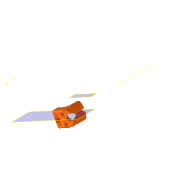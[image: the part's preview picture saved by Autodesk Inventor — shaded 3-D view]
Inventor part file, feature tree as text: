
AUTODESK INVENTOR PART (.ipt)
format: ipt  version: 2022 (Build 260153000, 153)  size: 468,992 bytes
history: native  units: in
note: dims shown in document units (in); Inventor stores cm internally (conversion verified against a paired STEP export)
features: sketch x13, extrude x9, other x8, reference x8, projected_geometry x3, plane x2, fillet x2, hole x2
ambient origin geometry x8: Origin, YZ Plane, XZ Plane, XY Plane, X Axis, Y Axis, Z Axis, Center Point
bodies: Solid1 (feature_tree)
feature tree (47):
  plane  "Work Plane1"
  extrude  "Extrusion1"  Depth=0.5307in
  sketch  "Skizze18"  dims[d23=0.2653in d25=135.0deg d26=0.1575in]
  plane  "Arbeitsebene3"
  other  "Arbeitsachse1"
  extrude  "Extrusion17"  TaperAngle=135.0deg  [1 undecoded]
  fillet  "Rundung4"  Radius=0.1575in
  hole  "Bohrung1"  [1 undecoded]
  extrude  "Extrusion19"  Depth=0.0591in
  hole  "Bohrung2"  [1 undecoded]
  extrude  "Extrusion20"  Depth=0.1181in
  extrude  "Extrusion21"  Depth=0.1102in
  extrude  "Extrusion22"  TaperAngle=0.0deg  [1 undecoded]
  fillet  "Rundung6"  Radius=0.4921in
  sketch  "Skizze27"  dims[d97=0.0in d98=0.0in d100=0.3937in d101=0.0in]
  extrude  "Extrusion23"  Depth=0.1575in
  extrude  "Extrusion24"  Depth=0.3937in TaperAngle=0.0deg
  extrude  "Extrusion25"  Depth=0.1575in
  sketch  "Sketch1"  dims[d0=1.1811in d1=0.0in d22=0.5307in]
  reference  "Reference1"
  sketch  "Skizze19"  dims[d27=0.2362in d29=0.3937in]
  reference  "Referenz6"
  sketch  "Skizze20"  dims[d31=0.5906in d40=0.0591in]
  reference  "Referenz7"
  reference  "Referenz8"
  sketch  "Skizze22"  dims[d42=1.378in d70=0.4724in]
  projected_geometry  "Projizierte Kontur13"
  projected_geometry  "Projizierte Kontur14"
  sketch  "Skizze23"  dims[d71=0.0in d72=-0.0069in d73=0.1181in]
  sketch  "Skizze24"  dims[d74=0.126in d75=0.2362in d76=0.2756in d77=1.1811in d78=90.0deg d79=0.315in d80=0.8108in d84=0.1102in]
  reference  "Referenz9"
  reference  "Referenz10"
  sketch  "Skizze25"  dims[d85=0.1102in d86=0.0in d87=0.0in d88=0.4921in]
  sketch  "Skizze26"  dims[d89=0.4921in d90=0.2362in d91=0.1575in d92=0.0787in d93=90.0deg d94=0.5118in d95=0.8108in d96=0.1575in]
  reference  "Referenz11"
  reference  "Referenz12"
  sketch  "Skizze28"  dims[d102=0.0in d103=0.0in d104=0.1575in]
  projected_geometry  "Projizierte Kontur15"
  sketch  "Skizze29"  dims[d105=0.6299in]
  sketch  "Skizze30"  dims[d106=0.6299in d107=0.1181in d108=0.1102in d109=0.1102in d110=0.0in d111=0.0in d112=45.0deg d113=0.0in d114=0.0in d115=0.1102in d116=0.1102in d117=0.3937in d118=0.0in]
  other  "<userpath>\Documents\Matchboxscope\INVENTOR\Matchboxscope_v0.iam"
  other  "Matchboxscope_v0.iam"
  other  "Matchboxscope_sample_v0:1"
  other  "Assembly_Matchboxscope_injectionmolded.iam"
  other  "IM_Matchboxscope_base_old:1"
  other  "IM_Matchboxscope_plate:2"
  other  "DIN 912 - ersetzt durch DIN EN ISO 4762 M3 x 25:2"
note: 4 required parameter values undecoded (feature->parameter linkage not recoverable at this tier; creation-order binding heuristic only, values carry confidence <= 0.55)
